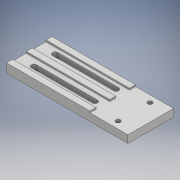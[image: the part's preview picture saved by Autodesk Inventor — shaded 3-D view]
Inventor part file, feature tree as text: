
AUTODESK INVENTOR PART (.ipt)
format: ipt  version: 2018 (Build 220112000, 112)  size: 159,744 bytes
history: native  units: mm
features: extrude x2, sketch x2, chamfer x1
ambient origin geometry x8: Origin, YZ Plane, XZ Plane, XY Plane, X Axis, Y Axis, Z Axis, Center Point
bodies: Solid1 (feature_tree)
feature tree (5):
  extrude  "Extrusion1"  Depth=11.0mm
  extrude  "Extrusion2"  Depth=1.0mm
  chamfer  "Chamfer1"  Distance=4.5mm
  sketch  "Sketch1"  dims[d0=21.0mm d1=11.0mm]
  sketch  "Sketch2"  dims[d2=30.0mm d3=3.0mm d4=4.5mm d5=80.0mm d6=3.5mm d7=3.5mm d8=10.0mm d10=10.0mm d11=8.0mm d12=8.0mm d13=18.875mm d14=18.875mm d15=5.0mm d16=0.0mm d17=4.0mm d18=4.0mm d19=4.0mm d20=55.0mm d21=1.0mm d22=0.0mm d23=2.0mm d24=2.0mm d25=45.0deg]
